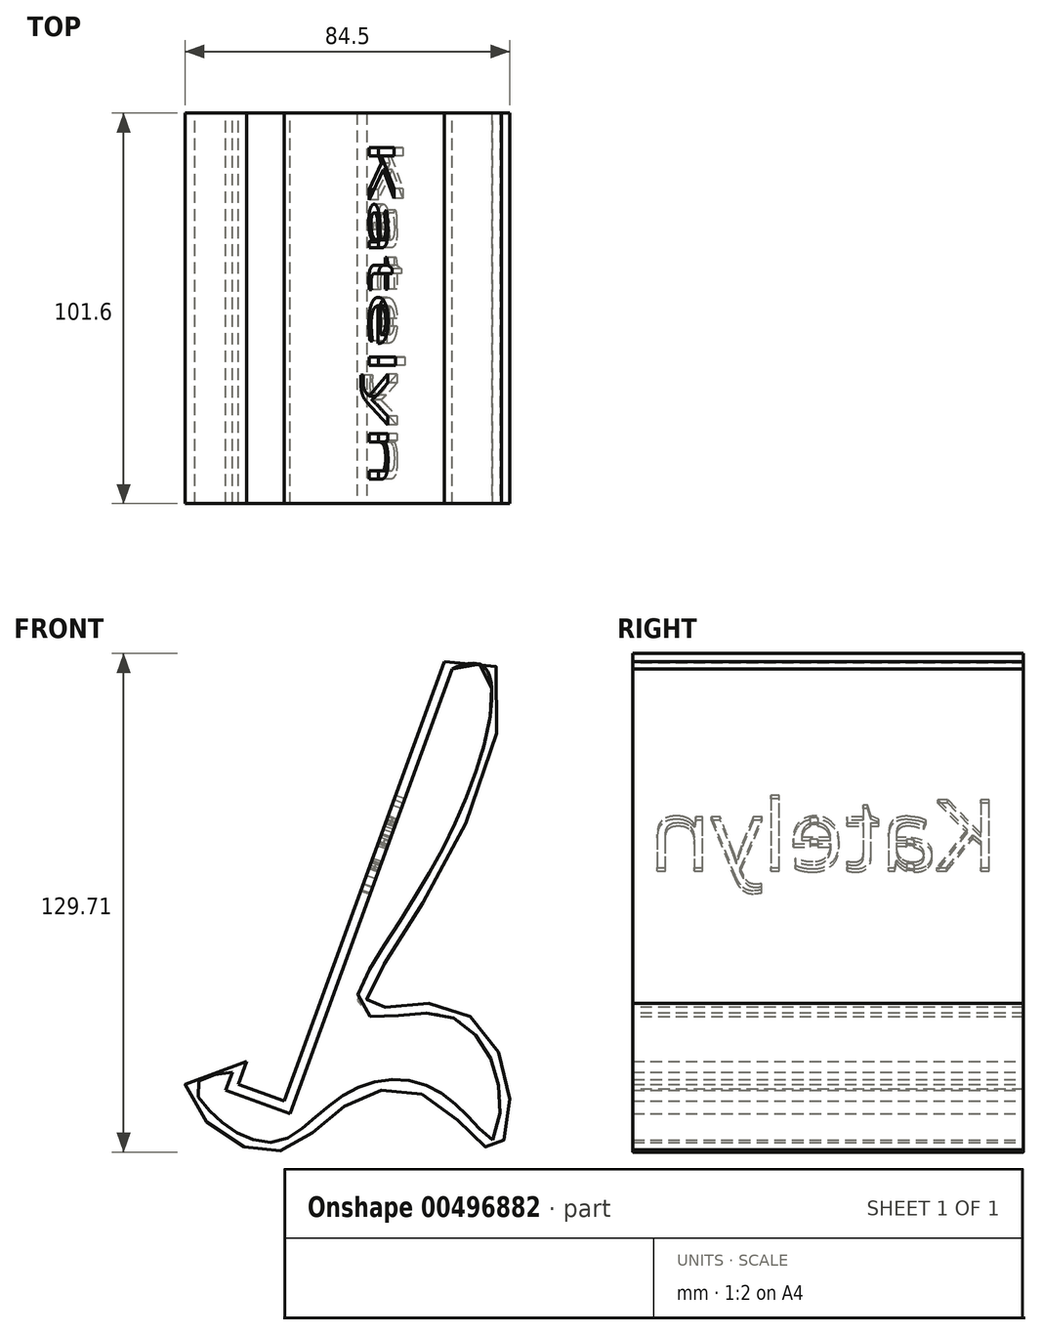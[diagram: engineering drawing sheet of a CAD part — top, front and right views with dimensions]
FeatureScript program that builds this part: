
annotation { "Feature Type Name" : "Feature", "Feature Type Description" : "" }
export const myFeature = defineFeature(function(context is Context, id is Id, definition is map)
    precondition{}
    {
        {
            var Q0;
            Q0=qCreatedBy(makeId("Front.planeOp"),FACE);
            var sketch = newSketch(context, id + "F0", { "sketchPlane" : qUnion([Q0])});
            skLineSegment(sketch, "E0.bottom", {"start": v(-76.2, 127) * mm, "end": v(0, 127) * mm, "construction": true});
            skLineSegment(sketch, "E0.top", {"start": v(-76.2, 0) * mm, "end": v(0, 0) * mm, "construction": true});
            skLineSegment(sketch, "E0.left", {"start": v(-76.2, 127) * mm, "end": v(-76.2, 0) * mm, "construction": true});
            skLineSegment(sketch, "E0.right", {"start": v(0, 127) * mm, "end": v(0, 0) * mm, "construction": true});
            skLineSegment(sketch, "E1", {"start": v(-22.66, 127) * mm, "end": v(-64.27, 12.7) * mm});
            skLineSegment(sketch, "E2", {"start": v(-64.27, 12.7) * mm, "end": v(-76.2, 17.04) * mm});
            skLineSegment(sketch, "E3", {"start": v(-76.2, 17.04) * mm, "end": v(-74.03, 23.01) * mm});
            skFitSpline(sketch, "E4", {"points": [v(-22.66, 127) * mm, v(-15.84, 87.6) * mm, v(-42.3, 37.7) * mm, v(-22.66, 37.7) * mm, v(-6, 17.04) * mm, v(-9.67, 0) * mm, v(-24.91, 12.7) * mm, v(-46.46, 12.7) * mm, v(-64.27, 0) * mm, v(-84.64, 7.46) * mm, v(-74.03, 23.01) * mm], "startDerivative": vector(503.22, 238.18) * mm, "endDerivative": vector(773.55, 27.46) * mm});
            skSolve(sketch);
        }
        {
            var Q0;
            Q0=qSketchRegion(id+"F0",true);
            extrude(context, id + "F1", {"entities" : qUnion([Q0]), "depth" : 101.6 * mm});
        }
        {
            var Q0;
            Q0=makeQuery(id+"F1.opExtrude","CAP_FACE",FACE,{"disambiguationData":[OSD([sQuery(id+"F0.wireOp",EDGE,"E1"),sQuery(id+"F0.wireOp",EDGE,"E2"),sQuery(id+"F0.wireOp",EDGE,"E3"),sQuery(id+"F0.wireOp",EDGE,"E4")])],"isStart":false});
            var Q1;
            Q1=makeQuery(id+"F1.opExtrude","CAP_FACE",FACE,{"disambiguationData":[OSD([sQuery(id+"F0.wireOp",EDGE,"E1"),sQuery(id+"F0.wireOp",EDGE,"E2"),sQuery(id+"F0.wireOp",EDGE,"E3"),sQuery(id+"F0.wireOp",EDGE,"E4")])],"isStart":true});
            shell(context, id + "F2", {"entities" : qUnion([Q0, Q1]), "thickness" : 2.54 * mm});
        }
        {
            var Q0;
            Q0=makeQuery(id+"F1.opExtrude","SWEPT_FACE",FACE,{"disambiguationData":[OSD([sQuery(id+"F0.wireOp",EDGE,"E1")])]});
            var sketch = newSketch(context, id + "F3", { "sketchPlane" : qUnion([Q0])});
            skText(sketch, "E5", { "text": "Katelyn\n", "fontName": "OpenSans-Regular.ttf"});
            skPoint(sketch, "E6", {"position": v(50.8, 111.59) * mm});
            const initialGuessF3  = {"E5": [0.00635, 0.05452, 1, 0, 0.01897]};
            skSetInitialGuess(sketch, initialGuessF3);
            skSolve(sketch);
        }
        {
            var Q0;
            Q0=qSketchRegion(id+"F3",true);
            extrude(context, id + "F4", {"entities" : qUnion([Q0]), "operationType" : NewBodyOperationType.REMOVE, "oppositeDirection" : true, "depth" : 2.54 * mm});
        }
        {
            var Q0;
            {var subQ2=sQuery(id+"F0.wireOp",EDGE,"E2");var subQ3=sQuery(id+"F0.wireOp",EDGE,"E1");Q0=makeQuery(id+"F4.boolean.opBoolean","SPLIT",FACE,{"disambiguationData":[TD([makeQuery(id+"F1.opExtrude","SWEPT_FACE",FACE,{"disambiguationData":[OSD([subQ2])]})])],"derivedFrom":makeQuery(id+"F1.opExtrude","SWEPT_FACE",FACE,{"disambiguationData":[OSD([subQ3])]})});}
            cPlane(context, id + "F5", {"entities" : qUnion([Q0]), "cplaneType" : CPlaneType.OFFSET, "offset" : 50.8 * mm, "oppositeDirection" : true, "width" : 152.4 * mm, "height" : 152.4 * mm});
        }
        {
            var Q0;
            {var subQ2=sQuery(id+"F0.wireOp",EDGE,"E2");var subQ3=sQuery(id+"F0.wireOp",EDGE,"E1");Q0=makeQuery(id+"F4.boolean.opBoolean","SPLIT",FACE,{"disambiguationData":[TD([makeQuery(id+"F2.opShell","OFFSET_FACE",FACE,{"disambiguationData":[OSD([subQ2])]})])],"derivedFrom":makeQuery(id+"F2.opShell","OFFSET_FACE",FACE,{"disambiguationData":[OSD([subQ3])]})});}
            var sketch = newSketch(context, id + "F6", { "sketchPlane" : qUnion([Q0])});
            skLineSegment(sketch, "E7.bottom", {"start": v(-28.5, 64.24) * mm, "end": v(-30.32, 64.24) * mm});
            skLineSegment(sketch, "E7.top", {"start": v(-28.5, 52.44) * mm, "end": v(-30.32, 52.44) * mm});
            skLineSegment(sketch, "E7.left", {"start": v(-28.5, 64.24) * mm, "end": v(-28.5, 52.44) * mm});
            skLineSegment(sketch, "E7.right", {"start": v(-30.32, 64.24) * mm, "end": v(-30.32, 52.44) * mm});
            skLineSegment(sketch, "E8.bottom", {"start": v(-53.42, 70.8) * mm, "end": v(-55.48, 70.8) * mm});
            skLineSegment(sketch, "E8.top", {"start": v(-53.42, 59.55) * mm, "end": v(-55.48, 59.55) * mm});
            skLineSegment(sketch, "E8.left", {"start": v(-53.42, 70.8) * mm, "end": v(-53.42, 59.55) * mm});
            skLineSegment(sketch, "E8.right", {"start": v(-55.48, 70.8) * mm, "end": v(-55.48, 59.55) * mm});
            skSolve(sketch);
        }
        {
            var Q0;
            Q0=qSketchRegion(id+"F6",true);
            extrude(context, id + "F7", {"entities" : qUnion([Q0]), "operationType" : NewBodyOperationType.ADD, "oppositeDirection" : true, "depth" : 1.27 * mm});
        }
    });
